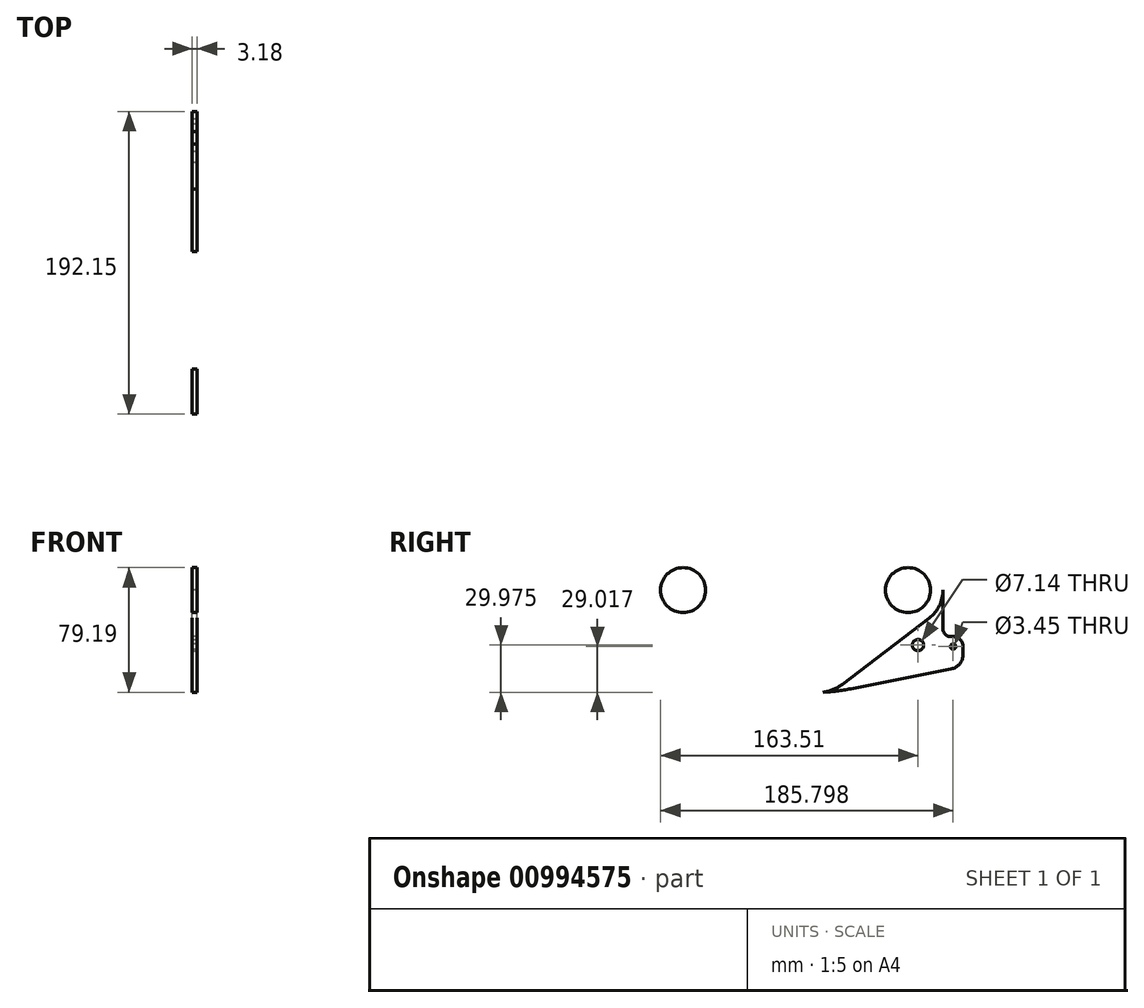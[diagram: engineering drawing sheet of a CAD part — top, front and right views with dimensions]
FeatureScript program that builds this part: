
annotation { "Feature Type Name" : "Feature", "Feature Type Description" : "" }
export const myFeature = defineFeature(function(context is Context, id is Id, definition is map)
    precondition{}
    {
        {
            var Q0;
            Q0=qCreatedBy(makeId("Right.planeOp"),FACE);
            var sketch = newSketch(context, id + "F0", { "sketchPlane" : qUnion([Q0])});
            skArc(sketch, "E0", {"start": v(0, 22.23) * mm, "mid": v(21.05, 7.12) * mm, "end": v(13.5, -17.66) * mm});
            skLineSegment(sketch, "E1", {"start": v(0, 22.23) * mm, "end": v(-142.88, 22.22) * mm});
            skLineSegment(sketch, "E2", {"start": v(-142.88, 22.22) * mm, "end": v(-142.88, -22.22) * mm, "construction": true});
            skLineSegment(sketch, "E3", {"start": v(-142.88, -22.22) * mm, "end": v(-101.6, -22.22) * mm});
            skLineSegment(sketch, "E4", {"start": v(-88.9, -34.92) * mm, "end": v(-88.9, -61.91) * mm});
            skArc(sketch, "E5", {"start": v(-142.88, 22.22) * mm, "mid": v(-165.1, 0) * mm, "end": v(-142.88, -22.22) * mm});
            skCircle(sketch, "E6", {"center": v(-142.88, 0) * mm, "radius": 14.29 * mm});
            skCircle(sketch, "E7", {"center": v(0, 0) * mm, "radius": 14.29 * mm});
            skPoint(sketch, "E8.visualSharp", {"position": v(-88.9, -22.22) * mm});
            skArc(sketch, "E8.filletArc", {"start": v(-88.9, -34.92) * mm, "mid": v(-92.62, -25.94) * mm, "end": v(-101.6, -22.22) * mm});
            skPoint(sketch, "E9.visualSharp", {"position": v(-88.9, -65.09) * mm});
            skLineSegment(sketch, "E10", {"start": v(-85.73, -65.09) * mm, "end": v(-57.15, -65.09) * mm});
            skLineSegment(sketch, "E11", {"start": v(-41.73, -59.87) * mm, "end": v(13.5, -17.66) * mm});
            skPoint(sketch, "E12.visualSharp", {"position": v(-48.55, -65.09) * mm});
            skArc(sketch, "E12.filletArc", {"start": v(-57.15, -65.09) * mm, "mid": v(-49, -63.75) * mm, "end": v(-41.73, -59.87) * mm});
            skArc(sketch, "E13.filletArc", {"start": v(-88.9, -61.91) * mm, "mid": v(-87.97, -64.16) * mm, "end": v(-85.73, -65.09) * mm});
            skLineSegment(sketch, "E14", {"start": v(-92.08, 82.32) * mm, "end": v(-92.08, -116.51) * mm, "construction": true});
            skPoint(sketch, "E15", {"position": v(-168.28, 0) * mm});
            skLineSegment(sketch, "E16", {"start": v(-107.62, -73.03) * mm, "end": v(-40.29, -73.03) * mm, "construction": true});
            skPoint(sketch, "E17", {"position": v(28.64, -35.88) * mm});
            skLineSegment(sketch, "E18", {"start": v(28.64, -35.88) * mm, "end": v(0, 0) * mm, "construction": true});
            skLineSegment(sketch, "E19", {"start": v(0, 0) * mm, "end": v(0, -19.4) * mm, "construction": true});
            skPoint(sketch, "E20.endSnap0", {"position": v(-71.44, -65.09) * mm});
            skLineSegment(sketch, "E21", {"start": v(28.64, -35.88) * mm, "end": v(28.64, 63.25) * mm, "construction": true});
            skLineSegment(sketch, "E22", {"start": v(28.64, -35.88) * mm, "end": v(26.26, -35.88) * mm, "construction": true});
            skLineSegment(sketch, "E23", {"start": v(26.26, -35.88) * mm, "end": v(26.26, 63.25) * mm, "construction": true});
            skLineSegment(sketch, "E24", {"start": v(26.26, 63.25) * mm, "end": v(28.64, 63.25) * mm, "construction": true});
            skLineSegment(sketch, "E25.MirrorCS", {"start": v(31.01, -35.88) * mm, "end": v(31.01, 63.25) * mm, "construction": true});
            skLineSegment(sketch, "E26.MirrorCS", {"start": v(31.01, 63.25) * mm, "end": v(28.64, 63.25) * mm, "construction": true});
            skLineSegment(sketch, "E27.MirrorCS", {"start": v(28.64, -35.88) * mm, "end": v(31.01, -35.88) * mm, "construction": true});
            skCircle(sketch, "E28", {"center": v(28.64, -35.88) * mm, "radius": 2.38 * mm, "construction": true});
            skLineSegment(sketch, "E29", {"start": v(-60.98, -65.09) * mm, "end": v(-57.15, -65.09) * mm});
            skLineSegment(sketch, "E30", {"start": v(-36.36, -62.68) * mm, "end": v(27.3, -50.1) * mm});
            skArc(sketch, "E31.filletArc", {"start": v(-60.98, -65.09) * mm, "mid": v(-48.61, -64.48) * mm, "end": v(-36.36, -62.68) * mm});
            skLineSegment(sketch, "E32", {"start": v(28.64, -29.53) * mm, "end": v(26.99, -29.53) * mm});
            skArc(sketch, "E33", {"start": v(22.22, -24.77) * mm, "mid": v(23.62, -28.14) * mm, "end": v(26.99, -29.53) * mm});
            skLineSegment(sketch, "E34.trimOffspring", {"start": v(22.23, -24.77) * mm, "end": v(22.23, 0) * mm});
            skArc(sketch, "E35", {"start": v(28.64, -29.53) * mm, "mid": v(33.13, -31.4) * mm, "end": v(34.99, -35.88) * mm});
            skLineSegment(sketch, "E36", {"start": v(34.99, -40.76) * mm, "end": v(34.99, -35.88) * mm});
            skPoint(sketch, "E37.visualSharp", {"position": v(34.99, -48.58) * mm});
            skArc(sketch, "E37.filletArc", {"start": v(27.3, -50.1) * mm, "mid": v(32.82, -46.8) * mm, "end": v(34.99, -40.76) * mm});
            skSolve(sketch);
        }
        {
            var Q0;
            Q0=makeQuery(id+"F0.imprint","IMPRINT",FACE,{"disambiguationData":[TD([[makeQuery(id+"F0.imprint","IMPRINT",EDGE,{"derivedFrom":sQuery(id+"F0.wireOp",EDGE,"E0")}),-1.0]])]});
            var Q1;
            Q1=makeQuery(id+"F0.imprint","IMPRINT",FACE,{"disambiguationData":[TD([[makeQuery(id+"F0.imprint","IMPRINT",EDGE,{"derivedFrom":sQuery(id+"F0.wireOp",EDGE,"E6")}),1.0]])]});
            var Q2;
            Q2=makeQuery(id+"F0.imprint","IMPRINT",FACE,{"disambiguationData":[TD([[makeQuery(id+"F0.imprint","IMPRINT",EDGE,{"derivedFrom":sQuery(id+"F0.wireOp",EDGE,"E7")}),1.0]])]});
            var Q3;
            {var subQ1=sQuery(id+"F0.wireOp",EDGE,"E11");Q3=makeQuery(id+"F0.imprint","IMPRINT",FACE,{"disambiguationData":[TD([[makeQuery(id+"F0.imprint","IMPRINT",EDGE,{"derivedFrom":subQ1}),-1.0]])]});}
            extrude(context, id + "F1", {"entities" : qUnion([Q0, Q1, Q2, Q3]), "depth" : 3.17 * mm, "offsetDistance" : 25.4 * mm});
        }
        {
            var Q0;
            Q0=makeQuery(id+"F1.opExtrude","CAP_FACE",FACE,{"disambiguationData":[OSD([sQuery(id+"F0.wireOp",EDGE,"E0"),sQuery(id+"F0.wireOp",EDGE,"E1"),sQuery(id+"F0.wireOp",EDGE,"E3"),sQuery(id+"F0.wireOp",EDGE,"E4"),sQuery(id+"F0.wireOp",EDGE,"kDeof0xj-KQPV-SBF1-FlAL-hYrGl1JxkNl2"),sQuery(id+"F0.wireOp",EDGE,"bW6pQdcF-bV7B-TQvH-agix-GGV9GthrlOmn"),sQuery(id+"F0.wireOp",EDGE,"E5"),sQuery(id+"F0.wireOp",EDGE,"74b1d450-59ad-4a02-9bfa-6329bbeba51b.filletArc"),sQuery(id+"F0.wireOp",EDGE,"E8.filletArc"),sQuery(id+"F0.wireOp",EDGE,"e2cd665b-0701-40c2-b96e-59d46e89fa53.filletArc")])],"isStart":false});
            var sketch = newSketch(context, id + "F2", { "sketchPlane" : qUnion([Q0])});
            skPoint(sketch, "E38", {"position": v(-142.88, 0) * mm});
            skPoint(sketch, "E39", {"position": v(0, 0) * mm});
            skSolve(sketch);
        }
        {
            var Q0;
            Q0=sQuery(id+"F2.wireOp",VERTEX,"E38");
            var Q1;
            Q1=sQuery(id+"F2.wireOp",VERTEX,"E39");
            var Q2;
            Q2=makeQuery(id+"F1.opExtrude","SWEPT_BODY",BODY,{"disambiguationData":[OSD([sQuery(id+"F0.wireOp",EDGE,"E0"),sQuery(id+"F0.wireOp",EDGE,"E1"),sQuery(id+"F0.wireOp",EDGE,"E3"),sQuery(id+"F0.wireOp",EDGE,"E4"),sQuery(id+"F0.wireOp",EDGE,"kDeof0xj-KQPV-SBF1-FlAL-hYrGl1JxkNl2"),sQuery(id+"F0.wireOp",EDGE,"bW6pQdcF-bV7B-TQvH-agix-GGV9GthrlOmn"),sQuery(id+"F0.wireOp",EDGE,"E5"),sQuery(id+"F0.wireOp",EDGE,"74b1d450-59ad-4a02-9bfa-6329bbeba51b.filletArc"),sQuery(id+"F0.wireOp",EDGE,"E8.filletArc"),sQuery(id+"F0.wireOp",EDGE,"e2cd665b-0701-40c2-b96e-59d46e89fa53.filletArc")])]});
            hole(context, id + "F3", {"style" : HoleStyle.SIMPLE, "endStyle" : HoleEndStyle.THROUGH, "holeDiameter" : 28.57 * mm, "majorDiameter" : 5 * mm, "isTappedThrough" : true, "tappedDepth" : 10.3 * mm, "tapClearance" : 3, "locations" : qUnion([Q0, Q1]), "scope" : qUnion([Q2])});
        }
        {
            var Q0;
            Q0=makeQuery(id+"F1.opExtrude","CAP_FACE",FACE,{"disambiguationData":[OSD([sQuery(id+"F0.wireOp",EDGE,"E0"),sQuery(id+"F0.wireOp",EDGE,"E1"),sQuery(id+"F0.wireOp",EDGE,"E3"),sQuery(id+"F0.wireOp",EDGE,"E4"),sQuery(id+"F0.wireOp",EDGE,"kDeof0xj-KQPV-SBF1-FlAL-hYrGl1JxkNl2"),sQuery(id+"F0.wireOp",EDGE,"bW6pQdcF-bV7B-TQvH-agix-GGV9GthrlOmn"),sQuery(id+"F0.wireOp",EDGE,"E5"),sQuery(id+"F0.wireOp",EDGE,"74b1d450-59ad-4a02-9bfa-6329bbeba51b.filletArc"),sQuery(id+"F0.wireOp",EDGE,"E8.filletArc"),sQuery(id+"F0.wireOp",EDGE,"e2cd665b-0701-40c2-b96e-59d46e89fa53.filletArc")])],"isStart":false});
            var sketch = newSketch(context, id + "F4", { "sketchPlane" : qUnion([Q0])});
            skPoint(sketch, "E40", {"position": v(-79.38, -33.34) * mm});
            skPoint(sketch, "E41", {"position": v(-79.38, -55.56) * mm});
            skArc(sketch, "E42", {"start": v(-79.38, -30.16) * mm, "mid": v(-82.55, -33.34) * mm, "end": v(-79.38, -36.51) * mm});
            skArc(sketch, "E43", {"start": v(-79.38, -52.39) * mm, "mid": v(-82.55, -55.56) * mm, "end": v(-79.38, -58.74) * mm});
            skArc(sketch, "E44", {"start": v(-53.98, -58.74) * mm, "mid": v(-50.8, -55.56) * mm, "end": v(-53.98, -52.39) * mm});
            skArc(sketch, "E45", {"start": v(-53.98, -36.51) * mm, "mid": v(-50.8, -33.34) * mm, "end": v(-53.98, -30.16) * mm});
            skLineSegment(sketch, "E46.bottom", {"start": v(-79.38, -36.51) * mm, "end": v(-53.98, -36.51) * mm});
            skLineSegment(sketch, "E46.top", {"start": v(-79.38, -30.16) * mm, "end": v(-53.98, -30.16) * mm});
            skLineSegment(sketch, "E47.bottom", {"start": v(-79.38, -52.39) * mm, "end": v(-53.98, -52.39) * mm});
            skLineSegment(sketch, "E47.top", {"start": v(-79.38, -58.74) * mm, "end": v(-53.98, -58.74) * mm});
            skSolve(sketch);
        }
        {
            var Q0;
            Q0=makeQuery(id+"F4.imprint","IMPRINT",FACE,{"disambiguationData":[TD([[makeQuery(id+"F4.imprint","IMPRINT",EDGE,{"derivedFrom":sQuery(id+"F4.wireOp",EDGE,"E42")}),1.0]])]});
            var Q1;
            Q1=makeQuery(id+"F4.imprint","IMPRINT",FACE,{"disambiguationData":[TD([[makeQuery(id+"F4.imprint","IMPRINT",EDGE,{"derivedFrom":sQuery(id+"F4.wireOp",EDGE,"E43")}),1.0]])]});
            extrude(context, id + "F5", {"entities" : qUnion([Q0, Q1]), "operationType" : NewBodyOperationType.REMOVE, "endBound" : BoundingType.THROUGH_ALL, "oppositeDirection" : true, "depth" : 25.4 * mm, "offsetDistance" : 25.4 * mm});
        }
        {
            var Q0;
            Q0=makeQuery(id+"F1.opExtrude","CAP_FACE",FACE,{"disambiguationData":[OSD([sQuery(id+"F0.wireOp",EDGE,"E0"),sQuery(id+"F0.wireOp",EDGE,"E1"),sQuery(id+"F0.wireOp",EDGE,"E3"),sQuery(id+"F0.wireOp",EDGE,"E4"),sQuery(id+"F0.wireOp",EDGE,"kDeof0xj-KQPV-SBF1-FlAL-hYrGl1JxkNl2"),sQuery(id+"F0.wireOp",EDGE,"bW6pQdcF-bV7B-TQvH-agix-GGV9GthrlOmn"),sQuery(id+"F0.wireOp",EDGE,"E5"),sQuery(id+"F0.wireOp",EDGE,"74b1d450-59ad-4a02-9bfa-6329bbeba51b.filletArc"),sQuery(id+"F0.wireOp",EDGE,"E8.filletArc"),sQuery(id+"F0.wireOp",EDGE,"e2cd665b-0701-40c2-b96e-59d46e89fa53.filletArc")])],"isStart":false});
            var sketch = newSketch(context, id + "F6", { "sketchPlane" : qUnion([Q0])});
            skLineSegment(sketch, "E48.bottom", {"start": v(-63.5, 21) * mm, "end": v(-19.05, 21) * mm, "construction": true});
            skLineSegment(sketch, "E48.top", {"start": v(-63.5, -21) * mm, "end": v(-19.05, -21) * mm, "construction": true});
            skLineSegment(sketch, "E48.left", {"start": v(-63.5, 21) * mm, "end": v(-63.5, -21) * mm, "construction": true});
            skLineSegment(sketch, "E48.right", {"start": v(-19.05, 21) * mm, "end": v(-19.05, -21) * mm, "construction": true});
            skLineSegment(sketch, "E49", {"start": v(-63.5, -21) * mm, "end": v(-19.05, 21) * mm, "construction": true});
            skPoint(sketch, "E50.middle", {"position": v(-41.28, 0) * mm});
            skPoint(sketch, "E51", {"position": v(-142.88, 0) * mm});
            skCircle(sketch, "E52", {"center": v(-41.28, 0) * mm, "radius": 25.4 * mm});
            skLineSegment(sketch, "E53", {"start": v(-63.5, 21) * mm, "end": v(-19.05, -21) * mm, "construction": true});
            skPoint(sketch, "E54", {"position": v(-59.73, 17.45) * mm});
            skPoint(sketch, "E55", {"position": v(-22.82, -17.45) * mm});
            skSolve(sketch);
        }
        {
            var Q0;
            Q0=sQuery(id+"F6.wireOp",VERTEX,"E50.top.end");
            var Q1;
            Q1=sQuery(id+"F6.wireOp",VERTEX,"E50.bottom.start");
            var Q2;
            Q2=sQuery(id+"F6.wireOp",VERTEX,"E54");
            var Q3;
            Q3=sQuery(id+"F6.wireOp",VERTEX,"E55");
            var Q4;
            Q4=makeQuery(id+"F1.opExtrude","SWEPT_BODY",BODY,{"disambiguationData":[OSD([sQuery(id+"F0.wireOp",EDGE,"E0"),sQuery(id+"F0.wireOp",EDGE,"E1"),sQuery(id+"F0.wireOp",EDGE,"E3"),sQuery(id+"F0.wireOp",EDGE,"E4"),sQuery(id+"F0.wireOp",EDGE,"kDeof0xj-KQPV-SBF1-FlAL-hYrGl1JxkNl2"),sQuery(id+"F0.wireOp",EDGE,"bW6pQdcF-bV7B-TQvH-agix-GGV9GthrlOmn"),sQuery(id+"F0.wireOp",EDGE,"E5"),sQuery(id+"F0.wireOp",EDGE,"74b1d450-59ad-4a02-9bfa-6329bbeba51b.filletArc"),sQuery(id+"F0.wireOp",EDGE,"E8.filletArc"),sQuery(id+"F0.wireOp",EDGE,"e2cd665b-0701-40c2-b96e-59d46e89fa53.filletArc")])]});
            hole(context, id + "F7", {"style" : HoleStyle.SIMPLE, "endStyle" : HoleEndStyle.THROUGH, "standardTappedOrClearance" : lookupTablePath({ "fit" : "Normal (ASME)", "standard" : "ANSI", "size" : "#8", "type" : "Clearance" }), "standardBlindInLast" : lookupTablePath({ "fit" : "Normal", "standard" : "ANSI", "engagement" : "75%", "pitch" : "32 tpi", "size" : "#8", "type" : "Clearance & tapped" }), "holeDiameter" : 4.98 * mm, "majorDiameter" : 6.35 * mm, "isTappedThrough" : true, "tappedDepth" : 10.3 * mm, "tapClearance" : 3, "locations" : qUnion([Q0, Q1, Q2, Q3]), "scope" : qUnion([Q4])});
        }
        {
            var Q0;
            Q0=sQuery(id+"F6.wireOp",VERTEX,"E50.middle");
            var Q1;
            Q1=makeQuery(id+"F1.opExtrude","SWEPT_BODY",BODY,{"disambiguationData":[OSD([sQuery(id+"F0.wireOp",EDGE,"E0"),sQuery(id+"F0.wireOp",EDGE,"E1"),sQuery(id+"F0.wireOp",EDGE,"E3"),sQuery(id+"F0.wireOp",EDGE,"E4"),sQuery(id+"F0.wireOp",EDGE,"kDeof0xj-KQPV-SBF1-FlAL-hYrGl1JxkNl2"),sQuery(id+"F0.wireOp",EDGE,"bW6pQdcF-bV7B-TQvH-agix-GGV9GthrlOmn"),sQuery(id+"F0.wireOp",EDGE,"E5"),sQuery(id+"F0.wireOp",EDGE,"74b1d450-59ad-4a02-9bfa-6329bbeba51b.filletArc"),sQuery(id+"F0.wireOp",EDGE,"E8.filletArc"),sQuery(id+"F0.wireOp",EDGE,"e2cd665b-0701-40c2-b96e-59d46e89fa53.filletArc")])]});
            hole(context, id + "F8", {"style" : HoleStyle.SIMPLE, "endStyle" : HoleEndStyle.THROUGH, "standardTappedOrClearance" : lookupTablePath({ "standard" : "ANSI", "size" : "13/16 (0.81)", "type" : "Drilled" }), "standardBlindInLast" : lookupTablePath({ "standard" : "ANSI", "size" : "13/16 (0.81)", "type" : "Drilled" }), "holeDiameter" : 13 / 406.4 * mm, "majorDiameter" : 6.35 * mm, "isTappedThrough" : true, "tappedDepth" : 19.05 * mm, "tapClearance" : 3, "locations" : qUnion([Q0]), "scope" : qUnion([Q1])});
        }
        {
            var Q0;
            Q0=makeQuery(id+"F1.opExtrude","CAP_FACE",FACE,{"disambiguationData":[OSD([sQuery(id+"F0.wireOp",EDGE,"E0"),sQuery(id+"F0.wireOp",EDGE,"E1"),sQuery(id+"F0.wireOp",EDGE,"E3"),sQuery(id+"F0.wireOp",EDGE,"E4"),sQuery(id+"F0.wireOp",EDGE,"kDeof0xj-KQPV-SBF1-FlAL-hYrGl1JxkNl2"),sQuery(id+"F0.wireOp",EDGE,"bW6pQdcF-bV7B-TQvH-agix-GGV9GthrlOmn"),sQuery(id+"F0.wireOp",EDGE,"E5"),sQuery(id+"F0.wireOp",EDGE,"74b1d450-59ad-4a02-9bfa-6329bbeba51b.filletArc"),sQuery(id+"F0.wireOp",EDGE,"E8.filletArc"),sQuery(id+"F0.wireOp",EDGE,"e2cd665b-0701-40c2-b96e-59d46e89fa53.filletArc")])],"isStart":false});
            var Q1;
            Q1=makeQuery(id+"F1.opExtrude","CAP_FACE",FACE,{"disambiguationData":[OSD([sQuery(id+"F0.wireOp",EDGE,"E0"),sQuery(id+"F0.wireOp",EDGE,"E1"),sQuery(id+"F0.wireOp",EDGE,"E3"),sQuery(id+"F0.wireOp",EDGE,"E4"),sQuery(id+"F0.wireOp",EDGE,"kDeof0xj-KQPV-SBF1-FlAL-hYrGl1JxkNl2"),sQuery(id+"F0.wireOp",EDGE,"bW6pQdcF-bV7B-TQvH-agix-GGV9GthrlOmn"),sQuery(id+"F0.wireOp",EDGE,"E5"),sQuery(id+"F0.wireOp",EDGE,"74b1d450-59ad-4a02-9bfa-6329bbeba51b.filletArc"),sQuery(id+"F0.wireOp",EDGE,"E8.filletArc"),sQuery(id+"F0.wireOp",EDGE,"e2cd665b-0701-40c2-b96e-59d46e89fa53.filletArc")])],"isStart":false});
            var sketch = newSketch(context, id + "F9", { "sketchPlane" : qUnion([Q0, Q1])});
            skPoint(sketch, "E56", {"position": v(-104.78, 0) * mm});
            skPoint(sketch, "E57", {"position": v(-142.88, 0) * mm});
            skPoint(sketch, "E58", {"position": v(6.35, -34.93) * mm});
            skSolve(sketch);
        }
        {
            var Q0;
            Q0=sQuery(id+"F9.wireOp",VERTEX,"E56");
            var Q1;
            Q1=sQuery(id+"F9.wireOp",VERTEX,"E58");
            var Q2;
            Q2=makeQuery(id+"F1.opExtrude","SWEPT_BODY",BODY,{"disambiguationData":[OSD([sQuery(id+"F0.wireOp",EDGE,"E0"),sQuery(id+"F0.wireOp",EDGE,"E1"),sQuery(id+"F0.wireOp",EDGE,"E3"),sQuery(id+"F0.wireOp",EDGE,"E4"),sQuery(id+"F0.wireOp",EDGE,"kDeof0xj-KQPV-SBF1-FlAL-hYrGl1JxkNl2"),sQuery(id+"F0.wireOp",EDGE,"bW6pQdcF-bV7B-TQvH-agix-GGV9GthrlOmn"),sQuery(id+"F0.wireOp",EDGE,"E5"),sQuery(id+"F0.wireOp",EDGE,"74b1d450-59ad-4a02-9bfa-6329bbeba51b.filletArc"),sQuery(id+"F0.wireOp",EDGE,"E8.filletArc"),sQuery(id+"F0.wireOp",EDGE,"e2cd665b-0701-40c2-b96e-59d46e89fa53.filletArc")])]});
            var Q3;
            Q3=makeQuery(id+"FBD7rU8Lc7J1awM_1.1.F1.opExtrude","SWEPT_BODY",BODY,{"disambiguationData":[OSD([sQuery(id+"F0.wireOp",EDGE,"E0"),sQuery(id+"F0.wireOp",EDGE,"E1"),sQuery(id+"F0.wireOp",EDGE,"E3"),sQuery(id+"F0.wireOp",EDGE,"E4"),sQuery(id+"F0.wireOp",EDGE,"kDeof0xj-KQPV-SBF1-FlAL-hYrGl1JxkNl2"),sQuery(id+"F0.wireOp",EDGE,"bW6pQdcF-bV7B-TQvH-agix-GGV9GthrlOmn"),sQuery(id+"F0.wireOp",EDGE,"E5"),sQuery(id+"F0.wireOp",EDGE,"74b1d450-59ad-4a02-9bfa-6329bbeba51b.filletArc"),sQuery(id+"F0.wireOp",EDGE,"E8.filletArc"),sQuery(id+"F0.wireOp",EDGE,"e2cd665b-0701-40c2-b96e-59d46e89fa53.filletArc")])]});
            hole(context, id + "F10", {"style" : HoleStyle.SIMPLE, "endStyle" : HoleEndStyle.THROUGH, "standardTappedOrClearance" : lookupTablePath({ "fit" : "Normal (ASME)", "standard" : "ANSI", "size" : "1/4", "type" : "Clearance" }), "standardBlindInLast" : lookupTablePath({ "fit" : "Normal", "standard" : "ANSI", "engagement" : "75%", "pitch" : "20 tpi", "size" : "1/4", "type" : "Clearance & tapped" }), "holeDiameter" : 7.14 * mm, "majorDiameter" : 6.35 * mm, "isTappedThrough" : true, "tappedDepth" : 19.05 * mm, "tapClearance" : 3, "locations" : qUnion([Q0, Q1]), "scope" : qUnion([Q2, Q3])});
        }
        {
            var Q0;
            Q0=sQuery(id+"F0.wireOp",VERTEX,"E17");
            var Q1;
            Q1=makeQuery(id+"F1.opExtrude","SWEPT_BODY",BODY,{"disambiguationData":[OSD([sQuery(id+"F0.wireOp",EDGE,"E0"),sQuery(id+"F0.wireOp",EDGE,"E1"),sQuery(id+"F0.wireOp",EDGE,"E3"),sQuery(id+"F0.wireOp",EDGE,"E4"),sQuery(id+"F0.wireOp",EDGE,"E5"),sQuery(id+"F0.wireOp",EDGE,"E8.filletArc"),sQuery(id+"F0.wireOp",EDGE,"E10"),sQuery(id+"F0.wireOp",EDGE,"E13.filletArc"),sQuery(id+"F0.wireOp",EDGE,"E20"),sQuery(id+"F0.wireOp",EDGE,"R3JIiJ8D-RaWP-1YYw-G5On-QH9ODOp8O3fn"),sQuery(id+"F0.wireOp",EDGE,"e943c5f5-722f-4070-aa30-f90368d2ee58.filletArc")])]});
            hole(context, id + "F11", {"style" : HoleStyle.SIMPLE, "endStyle" : HoleEndStyle.THROUGH, "oppositeDirection" : true, "standardTappedOrClearance" : lookupTablePath({ "standard" : "ANSI", "engagement" : "75%", "pitch" : "32 tpi", "size" : "#8", "type" : "Tapped" }), "standardBlindInLast" : lookupTablePath({ "standard" : "ANSI", "fit" : "Free", "engagement" : "75%", "pitch" : "32 tpi", "size" : "#8", "type" : "Clearance & tapped" }), "holeDiameter" : 3.45 * mm, "majorDiameter" : 4.17 * mm, "showTappedDepth" : true, "isTappedThrough" : true, "tappedDepth" : 10.3 * mm, "tapClearance" : 3, "locations" : qUnion([Q0]), "scope" : qUnion([Q1])});
        }
        {
            var Q0;
            Q0=qCreatedBy(makeId("Right.planeOp"),FACE);
            cPlane(context, id + "F12", {"entities" : qUnion([Q0]), "cplaneType" : CPlaneType.OFFSET, "offset" : 228.6 * mm, "oppositeDirection" : true, "width" : 152.4 * mm, "height" : 152.4 * mm});
        }
    });
